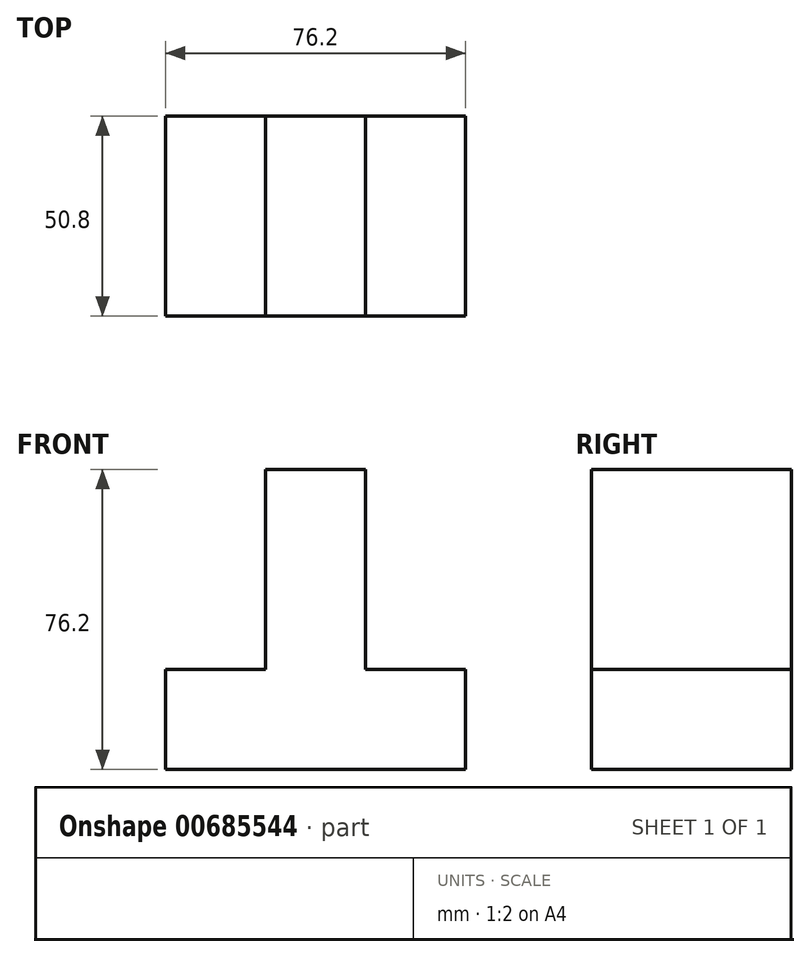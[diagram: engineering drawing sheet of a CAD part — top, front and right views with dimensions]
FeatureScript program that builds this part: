
annotation { "Feature Type Name" : "Feature", "Feature Type Description" : "" }
export const myFeature = defineFeature(function(context is Context, id is Id, definition is map)
    precondition{}
    {
        {
            var Q0;
            Q0=qCreatedBy(makeId("Front.planeOp"),FACE);
            var sketch = newSketch(context, id + "F0", { "sketchPlane" : qUnion([Q0])});
            skLineSegment(sketch, "E0", {"start": v(0, 0) * mm, "end": v(-76.2, 0) * mm});
            skLineSegment(sketch, "E1", {"start": v(-76.2, 0) * mm, "end": v(-76.2, 25.4) * mm});
            skLineSegment(sketch, "E2", {"start": v(-76.2, 25.4) * mm, "end": v(-50.8, 25.4) * mm});
            skLineSegment(sketch, "E3", {"start": v(-50.8, 25.4) * mm, "end": v(-50.8, 76.2) * mm});
            skLineSegment(sketch, "E4", {"start": v(-50.8, 76.2) * mm, "end": v(-25.4, 76.2) * mm});
            skLineSegment(sketch, "E5", {"start": v(-25.4, 76.2) * mm, "end": v(-25.4, 25.4) * mm});
            skLineSegment(sketch, "E6", {"start": v(-25.4, 25.4) * mm, "end": v(0, 25.4) * mm});
            skLineSegment(sketch, "E7", {"start": v(0, 25.4) * mm, "end": v(0, 0) * mm});
            skSolve(sketch);
        }
        {
            var Q0;
            Q0=makeQuery(id+"F0.imprint","IMPRINT",FACE,{"disambiguationData":[TD([[makeQuery(id+"F0.imprint","IMPRINT",EDGE,{"derivedFrom":sQuery(id+"F0.wireOp",EDGE,"E0")}),-1.0]])]});
            extrude(context, id + "F1", {"entities" : qUnion([Q0]), "depth" : 50.8 * mm, "offsetDistance" : 25.4 * mm});
        }
    });
